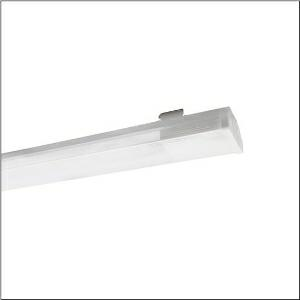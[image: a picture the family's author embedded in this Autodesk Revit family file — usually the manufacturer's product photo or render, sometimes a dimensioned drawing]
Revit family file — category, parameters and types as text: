
# Revit family: modario_r__31_gen_2_53bm8137u4f5c2_b53b
name_source: partatom
category: Lighting Fixtures
units: mm (PartAtom-declared; Revit-internal decimal feet)

## family parameters
Cut with Voids When Loaded = No
Host = Face
Light Source = No
Part Type = Normal
Room Calculation Point = No
Round Connector Dimension = Use Diameter
Shared = No

## types (1)
- Modario® 31 Gen.2 (1 x LED, 15990 lm, 90.4 W, 4000K)
    Apparent Load = 90 VA
    CIE Flux Codes = 62 83 95 93 100
    Color Rendering = 80
    Color Temperature = 4000K
    Default Elevation = 1800 mm
    Description = Modario® 31 Gen.2, luminaire insert, of sheet steel, coil coated, white, length: 2.392mm, width: 81mm, height: 82mm, 8x system unit, system units: 299mm, LED rated luminous flux: 15.990lm, light colour: 840, control gear: ON/OFF, with plug, 3-pole, with phase selection, mains connection: 220..240V, AC, 50/60Hz, rated input power: 90W, through-wiring accessed according to module size, primary optical cover: cover, of PMMA, light emission: direct distribution, primary light characteristic: symmetric, protection rating (complete): IP20, protection rating (LED compartment): IP50, insulation class (complete): insulation class I (protective earthing), certification: CE, ENEC, VDE, UKCA, impact resistance: IK03, permissible ambient temperature for indoor applications: -40..+40°C, corresponds to IFS (International Featured Standards) requirements for safety and quality in the food industry, reducing of maximum allowable ambient temperature of 5°C with ceiling mounting, packaging unit: 1 piece
    Height = 92 mm
    Lamp = 1 x LED
    Lamp Light Flux = 15990 lm
    Lamp Power = 90.4 W
    Lamp count = 1
    Length = 2392 mm
    Luminous efficacy = 177 lm/W
    Manufacturer = Siteco
    ModVariant = No
    Model = 53BM8137U4F5C2
    Mounting Place = Ceiling
    Mounting Type = Pendant
    Number of Poles = 1
    OnlyDefault = Yes
    Power Factor = 1
    Product Name = Modario® 31 Gen.2
    Product group = luminaire insert
    ProductGroupID = 902
    Protection Class = Protection class I
    Protection Degree = IP 20
    RLX_Detail_Level = 1
    RLX_Emergency_Light_Flux = 0 lm
    RLX_Emergency_Type = 0
    RLX_Emergency_Type_DB = No
    RlxData = <blob elided: 34745 chars, md5=7996fed2>
    Socket = socket
    Standby Power = 0 W
    System Light Flux = 15990 lm
    System Power = 90 W
    Type Comments = Product without accessories
    Type Image = l_1341883.jpg
    URL = http://relux.com
    VarID = ---
    Voltage = 0 V
    Weight = 0.00 kg
    Width = 81 mm

## geometry (parser evidence)
native form markers: Blend x4, Sweep x11
no freeform markers — native parametric forms only
